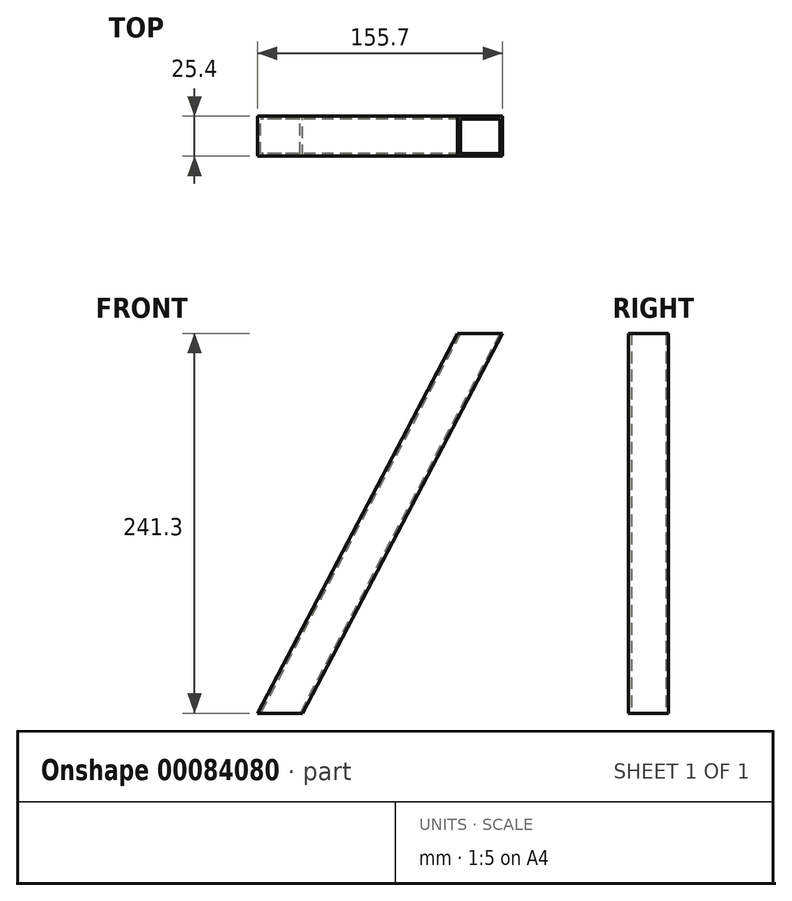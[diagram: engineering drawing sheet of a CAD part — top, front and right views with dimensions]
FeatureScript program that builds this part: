
annotation { "Feature Type Name" : "Feature", "Feature Type Description" : "" }
export const myFeature = defineFeature(function(context is Context, id is Id, definition is map)
    precondition{}
    {
        {
            var Q0;
            Q0=qCreatedBy(makeId("Front.planeOp"),FACE);
            var sketch = newSketch(context, id + "F0", { "sketchPlane" : qUnion([Q0])});
            skLineSegment(sketch, "E0", {"start": v(0, 0) * mm, "end": v(127, 241.3) * mm});
            skSolve(sketch);
        }
        {
            var Q0;
            Q0=sQuery(id+"F0.wireOp",EDGE,"E0");
            var Q1;
            Q1=sQuery(id+"F0.wireOp",VERTEX,"E0.start");
            cPlane(context, id + "F1", {"entities" : qUnion([Q0, Q1]), "cplaneType" : CPlaneType.CURVE_POINT, "offset" : 152.4 * mm, "width" : 152.4 * mm, "height" : 152.4 * mm});
        }
        {
            var Q0;
            Q0=qCreatedBy(id+"F1.planeOp",FACE);
            var sketch = newSketch(context, id + "F2", { "sketchPlane" : qUnion([Q0])});
            skLineSegment(sketch, "E1.rect.bottom", {"start": v(12.7, -12.7) * mm, "end": v(-12.7, -12.7) * mm});
            skLineSegment(sketch, "E1.rect.top", {"start": v(12.7, 12.7) * mm, "end": v(-12.7, 12.7) * mm});
            skLineSegment(sketch, "E1.rect.left", {"start": v(12.7, -12.7) * mm, "end": v(12.7, 12.7) * mm});
            skLineSegment(sketch, "E1.rect.right", {"start": v(-12.7, -12.7) * mm, "end": v(-12.7, 12.7) * mm});
            skPoint(sketch, "E1.rect.middle", {"position": v(0, 0) * mm});
            skLineSegment(sketch, "E2.rect.bottom", {"start": v(11.05, -11.05) * mm, "end": v(-11.05, -11.05) * mm});
            skLineSegment(sketch, "E2.rect.top", {"start": v(11.05, 11.05) * mm, "end": v(-11.05, 11.05) * mm});
            skLineSegment(sketch, "E2.rect.left", {"start": v(11.05, -11.05) * mm, "end": v(11.05, 11.05) * mm});
            skLineSegment(sketch, "E2.rect.right", {"start": v(-11.05, -11.05) * mm, "end": v(-11.05, 11.05) * mm});
            skSolve(sketch);
        }
        {
            var Q0;
            Q0=qCreatedBy(makeId("Top.planeOp"),FACE);
            cPlane(context, id + "F3", {"entities" : qUnion([Q0]), "cplaneType" : CPlaneType.OFFSET, "offset" : 241.3 * mm, "width" : 152.4 * mm, "height" : 152.4 * mm});
        }
        {
            var Q0;
            Q0=makeQuery(id+"F2.imprint","IMPRINT",FACE,{"disambiguationData":[TD([[makeQuery(id+"F2.imprint","IMPRINT",EDGE,{"derivedFrom":sQuery(id+"F2.wireOp",EDGE,"E1.rect.bottom")}),-1.0]])]});
            var Q1;
            Q1=qCreatedBy(id+"F3.planeOp",FACE);
            var Q2;
            Q2=qCreatedBy(makeId("Top.planeOp"),FACE);
            extrude(context, id + "F4", {"entities" : qUnion([Q0]), "endBound" : BoundingType.UP_TO_SURFACE, "endBoundEntityFace" : qUnion([Q1]), "depth" : 304.8 * mm, "hasSecondDirection" : true, "secondDirectionBound" : SecondDirectionBoundingType.UP_TO_SURFACE, "secondDirectionOppositeDirection" : true, "secondDirectionBoundEntityFace" : qUnion([Q2]), "secondDirectionDepth" : 25.4 * mm});
        }
    });
